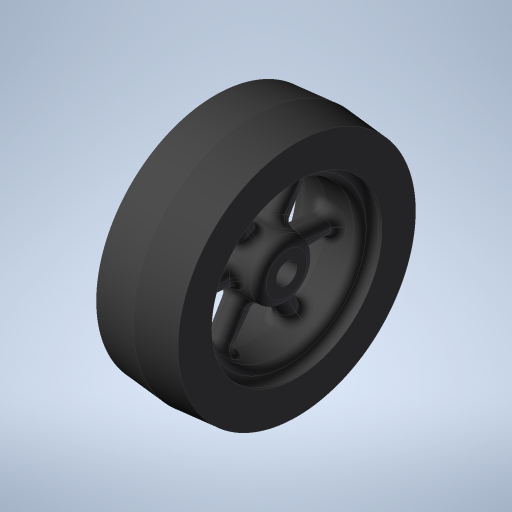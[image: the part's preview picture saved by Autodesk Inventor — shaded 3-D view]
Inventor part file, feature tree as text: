
AUTODESK INVENTOR PART (.ipt)
format: ipt  version: 2023 (Build 270158000, 158)  size: 1,292,288 bytes
history: native  units: in
note: dims shown in document units (in); Inventor stores cm internally (conversion verified against a paired STEP export)
features: extrude x3, sketch x2, fillet x2, draft x1
ambient origin geometry x8: Origin, YZ Plane, XZ Plane, XY Plane, X Axis, Y Axis, Z Axis, Center Point
bodies: Body1 (feature_tree)
feature tree (8):
  sketch  "Sketch1"  dims[d29=0.125in d31=2.0in d32=3.0in]
  extrude  "Extrusion7"  Depth=3.0in
  extrude  "Extrusion8"  Depth=0.1in
  extrude  "Extrusion9"  Depth=0.1in
  sketch  "Sketch3"  dims[d33=0.75in d34=0.25in d35=1.75in d37=2.3622in d39=360.0deg d41=1.0in d42=0.0in d43=0.75in d44=0.0in d45=0.25in d46=0.0in d54=0.0344in d55=0.1in d56=0.1in]
  draft  "FaceDraft2"
  fillet  "Fillet5"  Radius=2.3622in
  fillet  "Fillet6"  Radius=1.0in
